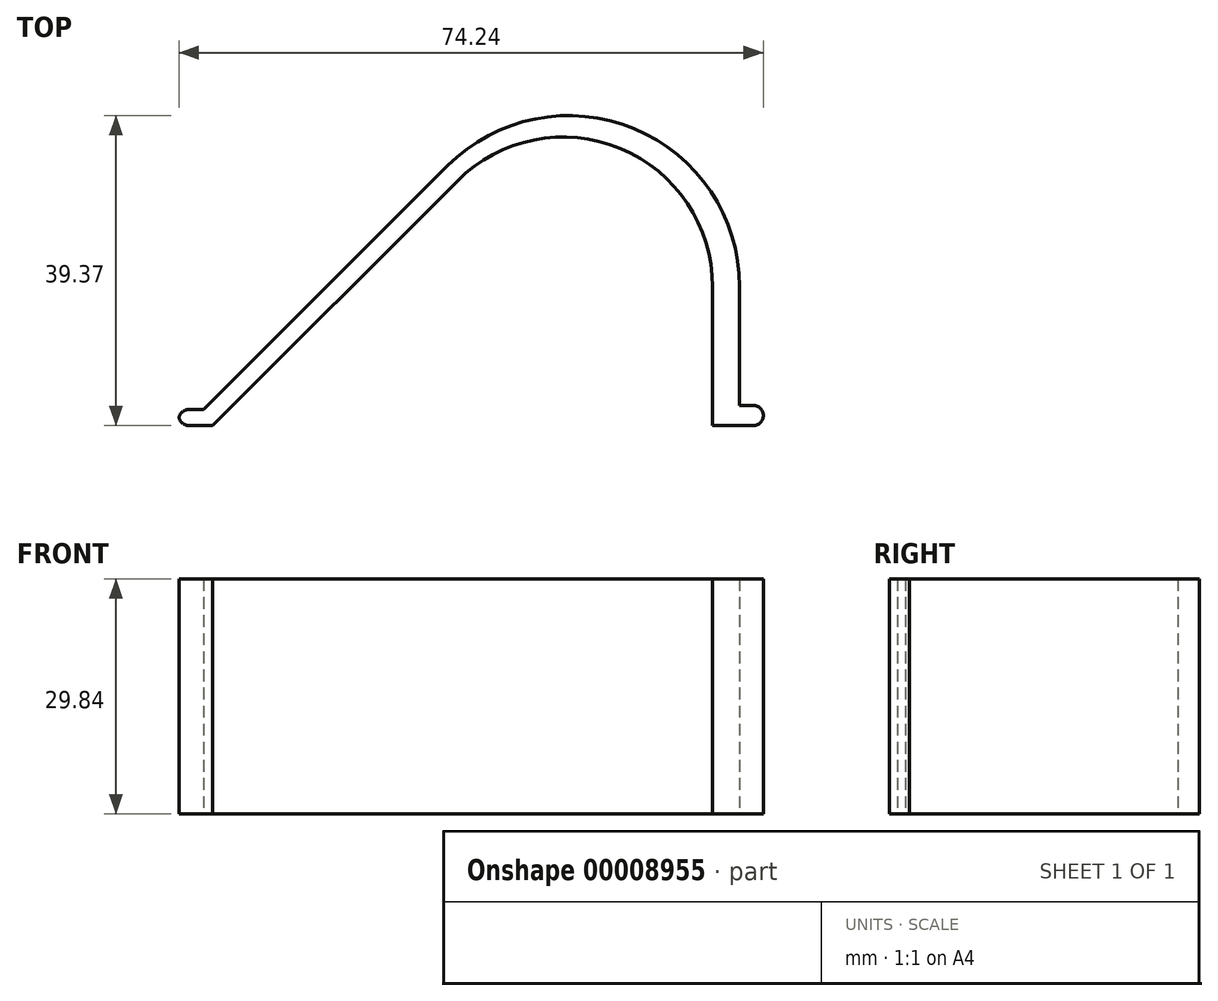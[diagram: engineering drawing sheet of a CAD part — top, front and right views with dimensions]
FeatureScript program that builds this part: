
annotation { "Feature Type Name" : "Feature", "Feature Type Description" : "" }
export const myFeature = defineFeature(function(context is Context, id is Id, definition is map)
    precondition{}
    {
        {
            var Q0;
            Q0=qCreatedBy(makeId("Top.planeOp"),FACE);
            var sketch = newSketch(context, id + "F0", { "sketchPlane" : qUnion([Q0])});
            skLineSegment(sketch, "E0", {"start": v(-49.66, 0) * mm, "end": v(48.8, 0) * mm, "construction": true});
            skLineSegment(sketch, "E1", {"start": v(38.2, 0) * mm, "end": v(38.2, 2.54) * mm});
            skLineSegment(sketch, "E2", {"start": v(38.2, 2.54) * mm, "end": v(35.18, 2.54) * mm});
            skLineSegment(sketch, "E3", {"start": v(35.18, 2.54) * mm, "end": v(35.18, 26.4) * mm});
            skLineSegment(sketch, "E4", {"start": v(31.75, 23.87) * mm, "end": v(31.75, 0) * mm});
            skLineSegment(sketch, "E5", {"start": v(31.75, 0) * mm, "end": v(38.2, 0) * mm});
            skPoint(sketch, "E6", {"position": v(-31.75, 0) * mm});
            skLineSegment(sketch, "E7", {"start": v(-31.75, 0) * mm, "end": v(-36.07, 0) * mm});
            skLineSegment(sketch, "E8", {"start": v(-36.07, 0) * mm, "end": v(-36.07, 2.03) * mm});
            skLineSegment(sketch, "E9", {"start": v(-36.07, 2.03) * mm, "end": v(-32.88, 2.03) * mm});
            skLineSegment(sketch, "E10", {"start": v(-32.88, 2.03) * mm, "end": v(1.78, 36.7) * mm});
            skLineSegment(sketch, "E11", {"start": v(-31.75, 0) * mm, "end": v(4.46, 36.2) * mm});
            skCircle(sketch, "E12", {"center": v(13.46, 17.65) * mm, "radius": 21.72 * mm});
            skCircle(sketch, "E13", {"center": v(12.76, 17.65) * mm, "radius": 19 * mm});
            skSolve(sketch);
        }
        {
            var Q0;
            {var subQ0=sQuery(id+"F0.wireOp",EDGE,"E12");var subQ2=sQuery(id+"F0.wireOp",EDGE,"E4");var subQ3=makeQuery(id+"F0.imprint","INTERSECT",VERTEX,{"derivedFrom":[subQ2,subQ0]});Q0=makeQuery(id+"F0.imprint","IMPRINT",FACE,{"disambiguationData":[TD([[makeQuery(id+"F0.imprint","IMPRINT",EDGE,{"disambiguationData":[TD([[subQ3,1.0]])],"derivedFrom":subQ2}),1.0]])]});}
            var Q1;
            Q1=makeQuery(id+"F0.imprint","IMPRINT",FACE,{"disambiguationData":[TD([[makeQuery(id+"F0.imprint","IMPRINT",EDGE,{"derivedFrom":sQuery(id+"F0.wireOp",EDGE,"E1")}),1.0]])]});
            var Q2;
            {var subQ4=sQuery(id+"F0.wireOp",EDGE,"E7");Q2=makeQuery(id+"F0.imprint","IMPRINT",FACE,{"disambiguationData":[TD([[makeQuery(id+"F0.imprint","IMPRINT",EDGE,{"derivedFrom":subQ4}),-1.0]])]});}
            extrude(context, id + "F1", {"entities" : qUnion([Q0, Q1, Q2]), "depth" : 29.84 * mm});
        }
        {
            var Q0;
            Q0=makeQuery(id+"F1.opExtrude","SWEPT_EDGE",EDGE,{"disambiguationData":[OSD([sQuery(id+"F0.wireOp",EDGE,"E1"),sQuery(id+"F0.wireOp",EDGE,"E2")])]});
            var Q1;
            Q1=makeQuery(id+"F1.opExtrude","SWEPT_EDGE",EDGE,{"disambiguationData":[OSD([sQuery(id+"F0.wireOp",EDGE,"E1"),sQuery(id+"F0.wireOp",EDGE,"E5")])]});
            var Q2;
            Q2=makeQuery(id+"F1.opExtrude","SWEPT_EDGE",EDGE,{"disambiguationData":[OSD([sQuery(id+"F0.wireOp",EDGE,"E8"),sQuery(id+"F0.wireOp",EDGE,"E9")])]});
            var Q3;
            Q3=makeQuery(id+"F1.opExtrude","SWEPT_EDGE",EDGE,{"disambiguationData":[OSD([sQuery(id+"F0.wireOp",EDGE,"E7"),sQuery(id+"F0.wireOp",EDGE,"E8")])]});
            fillet(context, id + "F2", {"entities" : qUnion([Q0, Q1, Q2, Q3]), "radius" : 1.27 * mm, "tangentPropagation" : true, "allowEdgeOverflow" : false});
        }
    });
